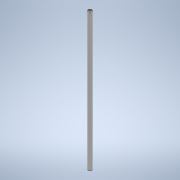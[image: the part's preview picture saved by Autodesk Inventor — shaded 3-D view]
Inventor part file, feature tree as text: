
AUTODESK INVENTOR PART (.ipt)
format: ipt  version: 2021 (Build 250183000, 183)  size: 94,208 bytes
history: native  units: mm
features: extrude x1, chamfer x1, sketch x1
ambient origin geometry x8: Origin, YZ Plane, XZ Plane, XY Plane, X Axis, Y Axis, Z Axis, Center Point
bodies: Solid1 (feature_tree)
feature tree (3):
  extrude  "Extrusion1"  Depth=300.0mm TaperAngle=0.0deg
  chamfer  "Chamfer1"  Distance=1.0mm Angle=45.0deg
  sketch  "Sketch1"  dims[d0=8.0mm d1=300.0mm d2=0.0mm d3=1.0mm d4=2.0mm d5=45.0deg]
